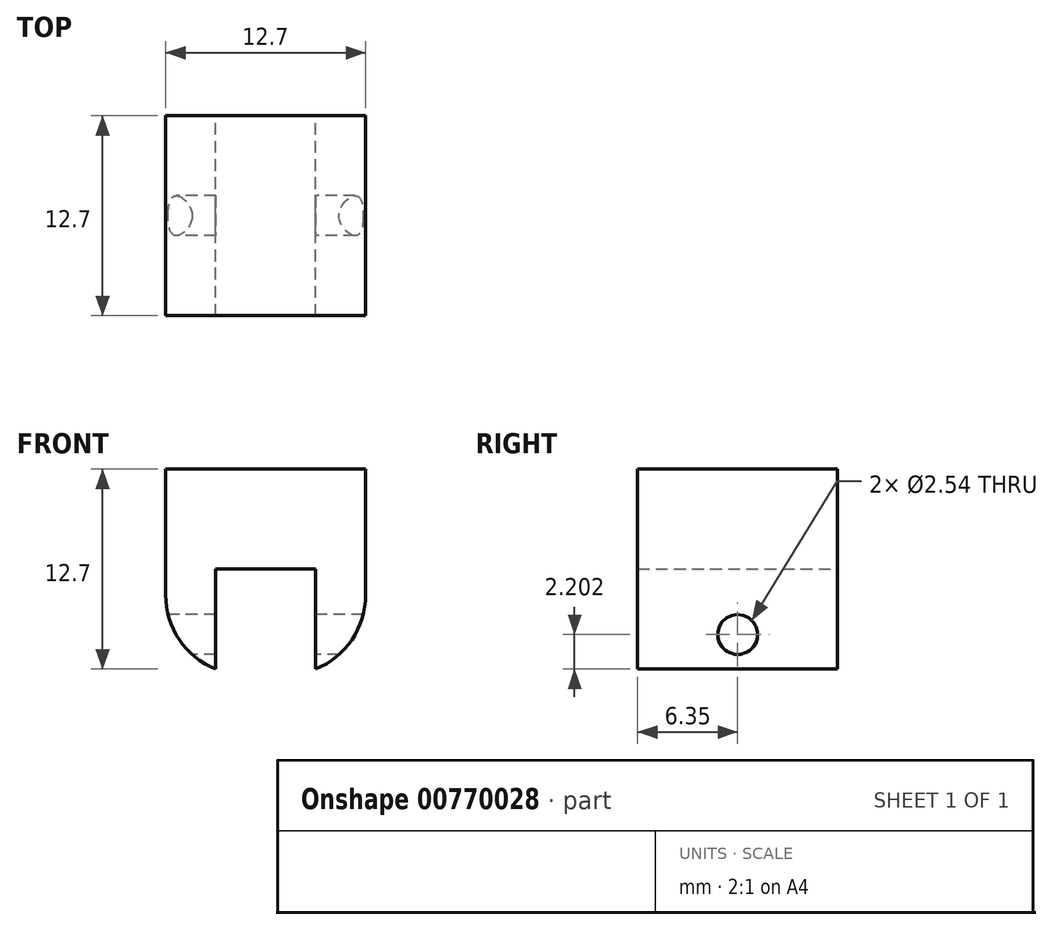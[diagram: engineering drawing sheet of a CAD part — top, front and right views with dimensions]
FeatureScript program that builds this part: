
annotation { "Feature Type Name" : "Feature", "Feature Type Description" : "" }
export const myFeature = defineFeature(function(context is Context, id is Id, definition is map)
    precondition{}
    {
        {
            var Q0;
            Q0=qCreatedBy(makeId("Top.planeOp"),FACE);
            var sketch = newSketch(context, id + "F0", { "sketchPlane" : qUnion([Q0])});
            skLineSegment(sketch, "E0.bottom", {"start": v(-6.35, 6.35) * mm, "end": v(6.35, 6.35) * mm});
            skLineSegment(sketch, "E0.top", {"start": v(-6.35, -6.35) * mm, "end": v(6.35, -6.35) * mm});
            skLineSegment(sketch, "E0.left", {"start": v(-6.35, 6.35) * mm, "end": v(-6.35, -6.35) * mm});
            skLineSegment(sketch, "E0.right", {"start": v(6.35, 6.35) * mm, "end": v(6.35, -6.35) * mm});
            skPoint(sketch, "E0.middle", {"position": v(0, 0) * mm});
            skSolve(sketch);
        }
        {
            var Q0;
            Q0 = qSketchRegion(id + "F0", true);
            extrude(context, id + "F1", {"entities" : qUnion([Q0]), "depth" : 12.7 * mm, "offsetDistance" : 25.4 * mm});
        }
        {
            var Q0;
            Q0=makeQuery(id+"F1.opExtrude","CAP_FACE",FACE,{"disambiguationData":[OSD([sQuery(id+"F0.wireOp",EDGE,"E0.bottom"),sQuery(id+"F0.wireOp",EDGE,"E0.top"),sQuery(id+"F0.wireOp",EDGE,"E0.left"),sQuery(id+"F0.wireOp",EDGE,"E0.right")])],"isStart":true});
            var sketch = newSketch(context, id + "F2", { "sketchPlane" : qUnion([Q0])});
            skLineSegment(sketch, "E1.bottom", {"start": v(-3.18, 17.55) * mm, "end": v(3.18, 17.55) * mm});
            skLineSegment(sketch, "E1.top", {"start": v(-3.18, -17.55) * mm, "end": v(3.18, -17.55) * mm});
            skLineSegment(sketch, "E1.left", {"start": v(-3.18, 17.55) * mm, "end": v(-3.18, -17.55) * mm});
            skLineSegment(sketch, "E1.right", {"start": v(3.18, 17.55) * mm, "end": v(3.18, -17.55) * mm});
            skPoint(sketch, "E1.middle", {"position": v(0, 0) * mm});
            skSolve(sketch);
        }
        {
            var Q0;
            Q0 = qSketchRegion(id + "F2", true);
            extrude(context, id + "F3", {"entities" : qUnion([Q0]), "operationType" : NewBodyOperationType.REMOVE, "oppositeDirection" : true, "depth" : 6.35 * mm, "offsetDistance" : 25.4 * mm});
        }
        {
            var Q0;
            Q0=makeQuery(id+"F1.opExtrude","SWEPT_FACE",FACE,{"disambiguationData":[OSD([sQuery(id+"F0.wireOp",EDGE,"E0.left")])]});
            var sketch = newSketch(context, id + "F4", { "sketchPlane" : qUnion([Q0])});
            skCircle(sketch, "E2", {"center": v(0, 2.2) * mm, "radius": 1.27 * mm});
            skSolve(sketch);
        }
        {
            var Q0;
            Q0 = qSketchRegion(id + "F4", true);
            extrude(context, id + "F5", {"entities" : qUnion([Q0]), "operationType" : NewBodyOperationType.REMOVE, "oppositeDirection" : true, "depth" : 25.4 * mm, "offsetDistance" : 25.4 * mm});
        }
        {
            var Q0;
            Q0=makeQuery(id+"F1.opExtrude","CAP_EDGE",EDGE,{"disambiguationData":[OSD([sQuery(id+"F0.wireOp",EDGE,"E0.left")])],"isStart":true});
            var Q1;
            Q1=makeQuery(id+"F1.opExtrude","CAP_EDGE",EDGE,{"disambiguationData":[OSD([sQuery(id+"F0.wireOp",EDGE,"E0.right")])],"isStart":true});
            fillet(context, id + "F6", {"entities" : qUnion([Q0, Q1]), "radius" : 5.08 * mm, "tangentPropagation" : true, "allowEdgeOverflow" : false});
        }
    });
